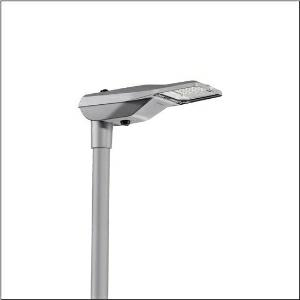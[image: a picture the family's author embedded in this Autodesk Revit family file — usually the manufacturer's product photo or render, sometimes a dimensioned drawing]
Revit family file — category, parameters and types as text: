
# Revit family: streetlight_sl_21_micro___st1_5a_5xe1p33t08db_27e3
name_source: partatom
category: Lighting Fixtures
units: mm (PartAtom-declared; Revit-internal decimal feet)

## family parameters
Cut with Voids When Loaded = No
Host = Face
Light Source = No
Part Type = Normal
Room Calculation Point = No
Round Connector Dimension = Use Diameter
Shared = No

## types (1)
- --- (1 x LED, 5020 lm, 39.1 W, 3000K)
    Apparent Load = 39 VA
    CIE Flux Codes = 22 53 95 100 100
    Color Rendering = 70
    Color Temperature = 3000K
    Default Elevation = 1800 mm
    Description = Streetlight SL 21 micro, mast luminaire, primary light control with lens, of PMMA, primary optical cover: cover, of toughened safety glass, transparent, light distribution: ST1.5a, light emission: direct distribution, primary light characteristic: asymmetric, installation type: side-entry, post-top, LED, High Power LED, rated luminous flux: 5.020lm, luminous efficacy: 128lm/W, light colour: 730, colour temperature: 3000K, control gear: D4i, control: flexible luminous flux parameterisation, time-dependent luminous flux control, constant luminous flux control, overheat protection, pre-setting: logarithmic dimming characteristic, mains connection: 220..240V, AC, 50/60Hz, start of lifetime: 39W, end of service life: 41W, reduction: 18W, luminaire housing, of diecast aluminium, powder-coated, SITECO metallic grey (DB 702S), corrosivity category C5 high according to DIN EN ISO 12944, please order mast flange separately, inclination adjustable: 0°, 5°, 10°, 15°, sealing non-destructively replaceable, multi-level sealing system, length: 528mm, width: 235mm, height: 110mm, mast flange for spigot size: 42mm (side-entry): 5XC10008XM4, 60/48mm (side-entry/post-top): 5XC10108XM2, 76/60mm (side-entry/post-top): 5XC10108XM1, Smart Interface below and above, protection rating (complete): IP66, insulation class (complete): insulation class II (safety insulation), certification: CE, ENEC, ENEC+, VDE, impact resistance: IK10, permissible operating ambient temperature for outdoor applications: -40..+50°C, standard-compliant lighting for roads and squares, packaging unit: 1 piece

Light Distribution: ST1.5a
    Height = 110 mm
    Lamp = 1 x LED
    Lamp Light Flux = 5020 lm
    Lamp Power = 39.1 W
    Lamp count = 1
    Length = 528 mm
    Luminous efficacy = 128 lm/W
    Manufacturer = Siteco
    ModVariant = No
    Model = 5XE1P33T08DB
    Number of Poles = 1
    OnlyDefault = Yes
    Power Factor = 1
    Product Name = Streetlight SL 21 micro | ST1.5a
    Product group = mast luminaire | pylon top
    ProductGroupID = 6100
    Protection Class = Protection class II
    Protection Degree = IP 66
    RLX_Detail_Level = 1
    RLX_Emergency_Light_Flux = 0 lm
    RLX_Emergency_Type = 0
    RLX_Emergency_Type_DB = No
    RlxData = <blob elided: 102505 chars, md5=a505f2b6>
    Socket = socket
    Standby Power = 0 W
    System Light Flux = 5020 lm
    System Power = 39 W
    Type Comments = factory setting: luminous flux: 100 % | dim-lin: 254 | 765 mA
    Type Image = l_1007239.jpg
    URL = http://relux.com
    VarID = @adj_153165
    Voltage = 0 V
    Weight = 0.00 kg
    Width = 235 mm

## geometry (parser evidence)
native form markers: Blend x4, Sweep x11
no freeform markers — native parametric forms only
